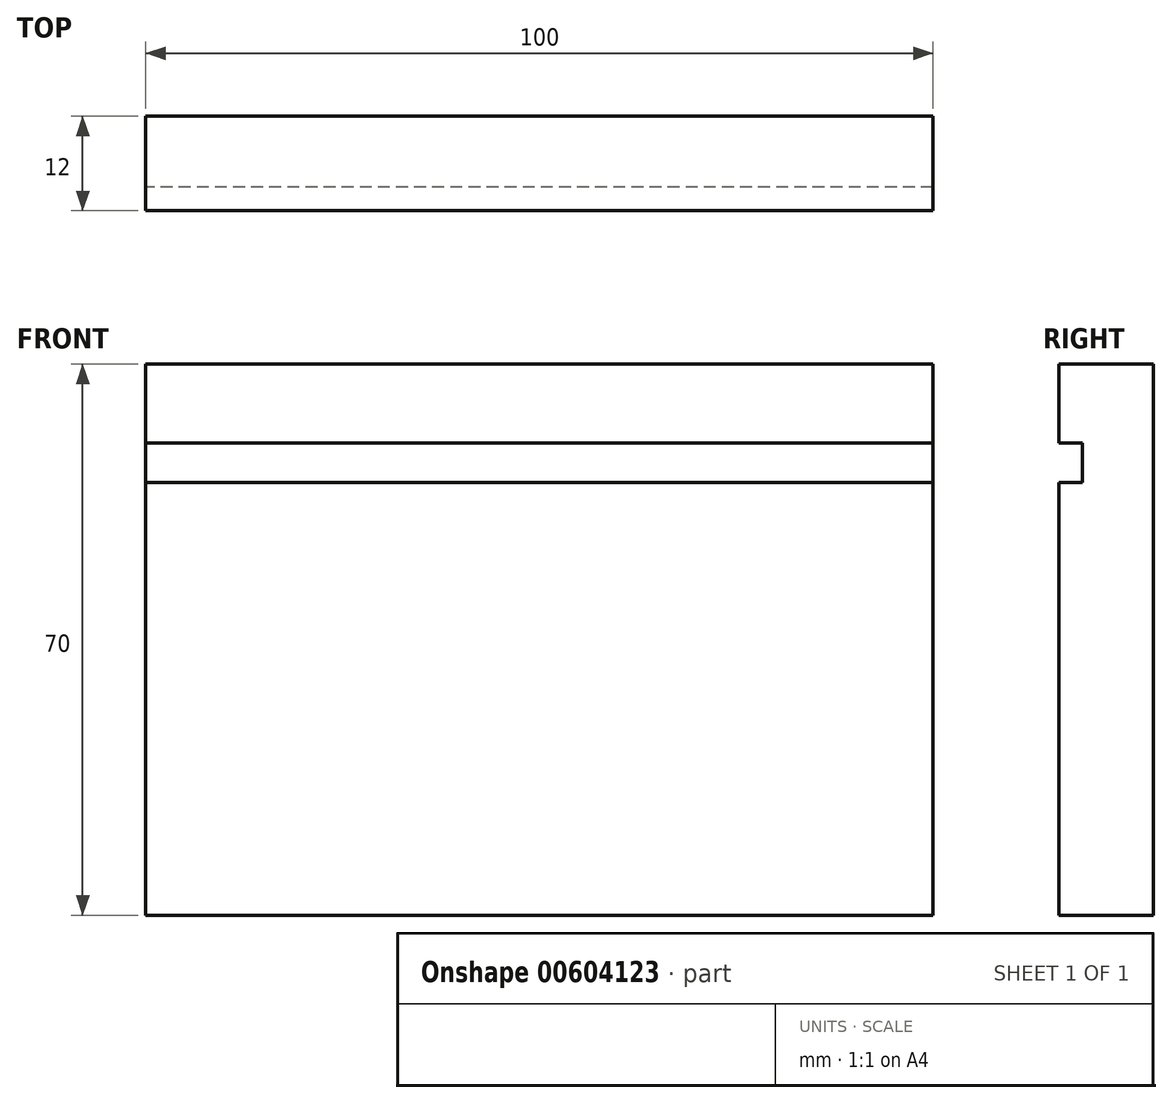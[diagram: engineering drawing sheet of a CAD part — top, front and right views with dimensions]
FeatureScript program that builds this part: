
annotation { "Feature Type Name" : "Feature", "Feature Type Description" : "" }
export const myFeature = defineFeature(function(context is Context, id is Id, definition is map)
    precondition{}
    {
        {
            var Q0;
            Q0=qCreatedBy(makeId("Right.planeOp"),FACE);
            var sketch = newSketch(context, id + "F0", { "sketchPlane" : qUnion([Q0])});
            skLineSegment(sketch, "E0", {"start": v(0, 0) * mm, "end": v(0, 70) * mm});
            skLineSegment(sketch, "E1", {"start": v(0, 70) * mm, "end": v(-12, 70) * mm});
            skLineSegment(sketch, "E2", {"start": v(-12, 70) * mm, "end": v(-12, 60) * mm});
            skLineSegment(sketch, "E3", {"start": v(-12, 60) * mm, "end": v(-9, 60) * mm});
            skLineSegment(sketch, "E4", {"start": v(-9, 60) * mm, "end": v(-9, 55) * mm});
            skLineSegment(sketch, "E5", {"start": v(-9, 55) * mm, "end": v(-12, 55) * mm});
            skLineSegment(sketch, "E6", {"start": v(-12, 55) * mm, "end": v(-12, 1.87) * mm});
            skLineSegment(sketch, "E7", {"start": v(0, 0) * mm, "end": v(-12, 0) * mm});
            skLineSegment(sketch, "E8", {"start": v(-12, 1.87) * mm, "end": v(-12, 0) * mm});
            skSolve(sketch);
        }
        {
            var Q0;
            Q0 = qSketchRegion(id + "F0", true);
            extrude(context, id + "F1", {"entities" : qUnion([Q0]), "depth" : 900 * mm, "offsetDistance" : 25 * mm});
        }
        {
            var Q0;
            Q0=makeQuery(id+"F1.opExtrude","SWEPT_FACE",FACE,{"disambiguationData":[OSD([sQuery(id+"F0.wireOp",EDGE,"E6"),sQuery(id+"F0.wireOp",EDGE,"E8")])]});
            var sketch = newSketch(context, id + "F2", { "sketchPlane" : qUnion([Q0])});
            skLineSegment(sketch, "E9.bottom", {"start": v(900, 0) * mm, "end": v(100, 0) * mm});
            skLineSegment(sketch, "E9.top", {"start": v(900, 409.44) * mm, "end": v(100, 409.44) * mm});
            skLineSegment(sketch, "E9.left", {"start": v(900, 0) * mm, "end": v(900, 409.44) * mm});
            skLineSegment(sketch, "E9.right", {"start": v(100, 0) * mm, "end": v(100, 409.44) * mm});
            skSolve(sketch);
        }
        {
            var Q0;
            Q0 = qSketchRegion(id + "F2", true);
            extrude(context, id + "F3", {"entities" : qUnion([Q0]), "operationType" : NewBodyOperationType.REMOVE, "oppositeDirection" : true, "depth" : 25 * mm, "offsetDistance" : 25 * mm});
        }
    });
